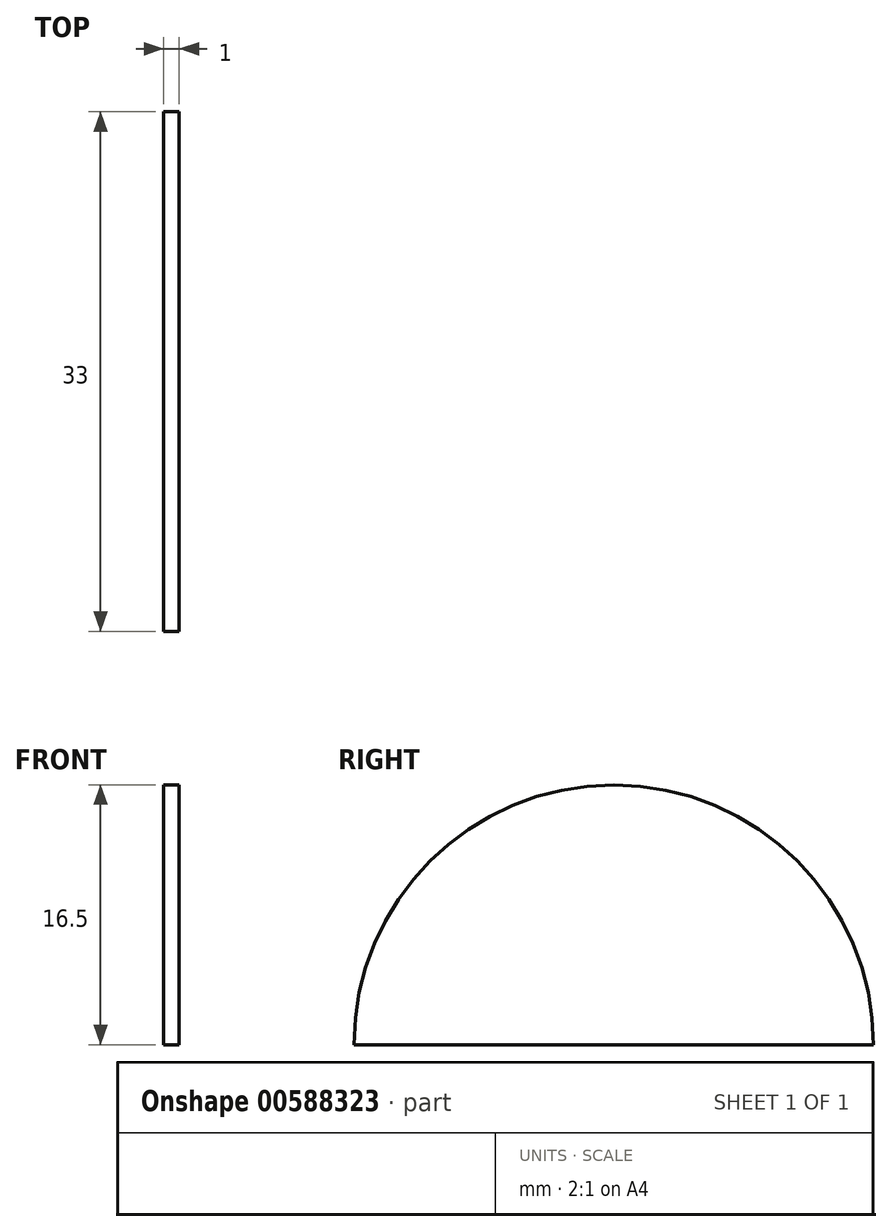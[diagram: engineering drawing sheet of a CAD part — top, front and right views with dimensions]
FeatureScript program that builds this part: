
annotation { "Feature Type Name" : "Feature", "Feature Type Description" : "" }
export const myFeature = defineFeature(function(context is Context, id is Id, definition is map)
    precondition{}
    {
        {
            var Q0;
            Q0=qCreatedBy(makeId("Right.planeOp"),FACE);
            var sketch = newSketch(context, id + "F0", { "sketchPlane" : qUnion([Q0])});
            skLineSegment(sketch, "E0", {"start": v(-54.62, 17.63) * mm, "end": v(4.05, 17.63) * mm});
            skLineSegment(sketch, "E1", {"start": v(4.05, 17.63) * mm, "end": v(-25.29, 17.63) * mm});
            skArc(sketch, "E2", {"start": v(-8.79, 17.63) * mm, "mid": v(-25.29, 34.13) * mm, "end": v(-41.79, 17.63) * mm});
            skSolve(sketch);
        }
        {
            var Q0;
            {var subQ3=sQuery(id+"F0.wireOp",EDGE,"E2");Q0=makeQuery(id+"F0.imprint","IMPRINT",FACE,{"disambiguationData":[TD([[makeQuery(id+"F0.imprint","IMPRINT",EDGE,{"derivedFrom":subQ3}),1.0]])]});}
            extrude(context, id + "F1", {"entities" : qUnion([Q0]), "depth" : 1 * mm, "offsetDistance" : 25 * mm});
        }
    });
